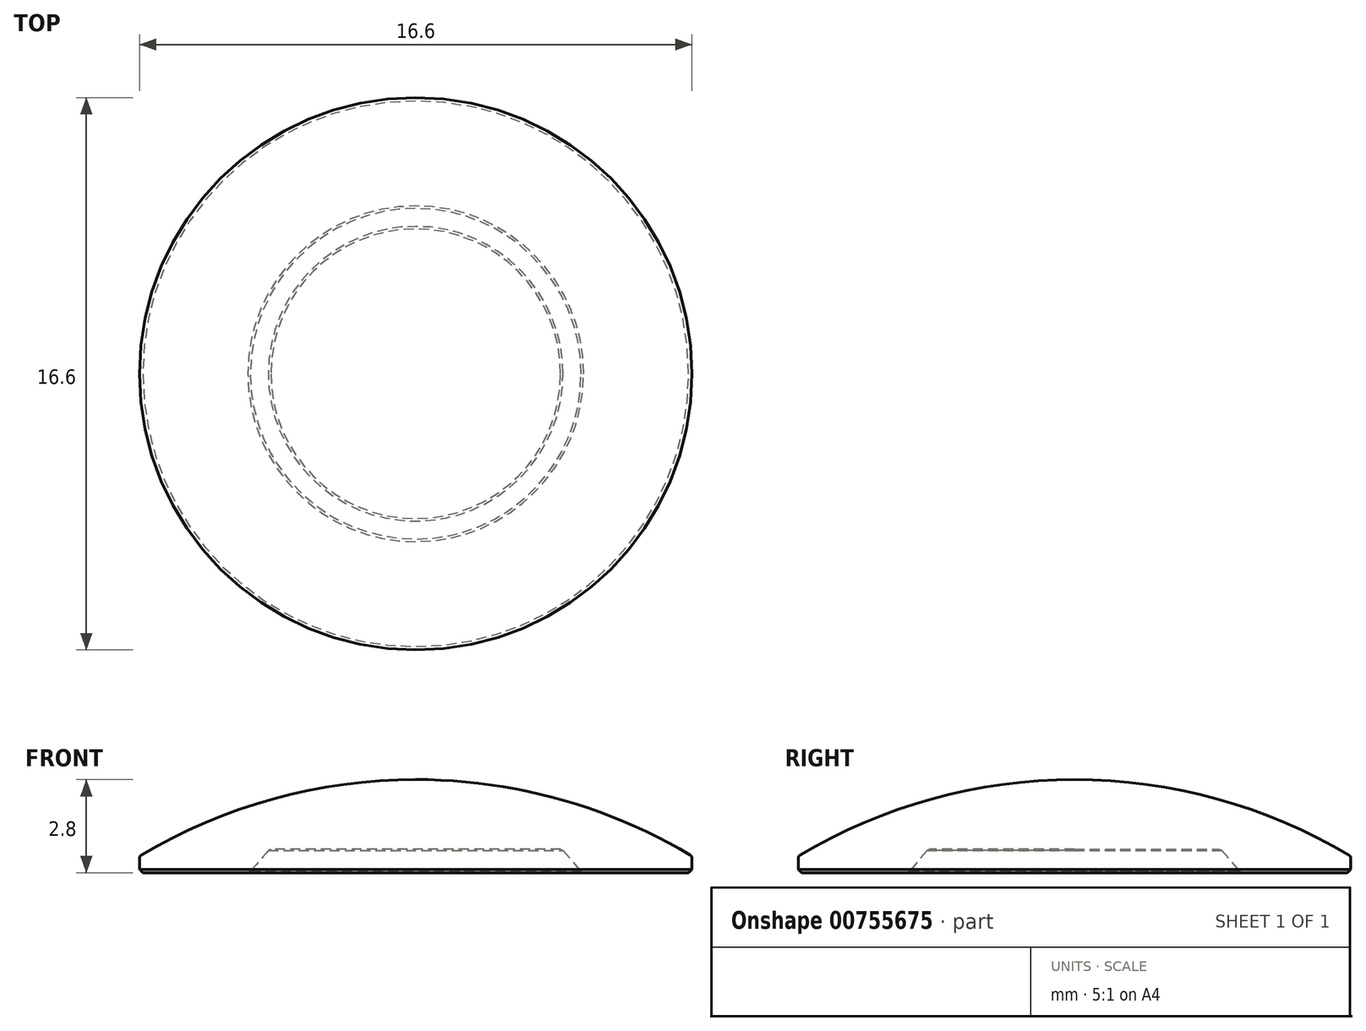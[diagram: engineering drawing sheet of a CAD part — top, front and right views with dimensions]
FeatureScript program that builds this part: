
annotation { "Feature Type Name" : "Feature", "Feature Type Description" : "" }
export const myFeature = defineFeature(function(context is Context, id is Id, definition is map)
    precondition{}
    {
        {
            var Q0;
            Q0=qCreatedBy(makeId("Front.planeOp"),FACE);
            var sketch = newSketch(context, id + "F0", { "sketchPlane" : qUnion([Q0])});
            skLineSegment(sketch, "E0", {"start": v(0, 2.8) * mm, "end": v(12.91, 2.8) * mm, "construction": true});
            skLineSegment(sketch, "E1", {"start": v(8.3, 0) * mm, "end": v(8.3, 0.5) * mm});
            skArc(sketch, "E2", {"start": v(8.3, 0.5) * mm, "mid": v(4.3, 2.21) * mm, "end": v(0, 2.8) * mm});
            skLineSegment(sketch, "E3", {"start": v(8.3, 0) * mm, "end": v(5, 0) * mm});
            skLineSegment(sketch, "E4", {"start": v(0, 2.8) * mm, "end": v(0, 0.7) * mm});
            skLineSegment(sketch, "E5", {"start": v(0, 0.7) * mm, "end": v(4.4, 0.7) * mm});
            skLineSegment(sketch, "E6", {"start": v(4.4, 0.7) * mm, "end": v(5, 0) * mm});
            skLineSegment(sketch, "E7", {"start": v(0, 4.27) * mm, "end": v(0, -3.75) * mm, "construction": true});
            skSolve(sketch);
        }
        {
            var Q0;
            Q0=makeQuery(id+"F0.imprint","IMPRINT",FACE,{"disambiguationData":[TD([[makeQuery(id+"F0.imprint","IMPRINT",EDGE,{"derivedFrom":sQuery(id+"F0.wireOp",EDGE,"E1")}),1.0]])]});
            var Q1;
            Q1=sQuery(id+"F0.wireOp",EDGE,"E7");
            revolve(context, id + "F1", {"surfaceOperationType" : NewSurfaceOperationType.NEW, "entities" : qUnion([Q0]), "axis" : qUnion([Q1]), "revolveType" : RevolveType.FULL});
        }
        {
            var Q0;
            Q0=makeQuery(id+"F1.opRevolve","SWEPT_EDGE",EDGE,{"disambiguationData":[OSD([sQuery(id+"F0.wireOp",EDGE,"E1"),sQuery(id+"F0.wireOp",EDGE,"E3")])]});
            var Q1;
            Q1=makeQuery(id+"F1.opRevolve","SWEPT_EDGE",EDGE,{"disambiguationData":[OSD([sQuery(id+"F0.wireOp",EDGE,"E3"),sQuery(id+"F0.wireOp",EDGE,"E6")])]});
            var Q2;
            Q2=makeQuery(id+"F1.opRevolve","SWEPT_EDGE",EDGE,{"disambiguationData":[OSD([sQuery(id+"F0.wireOp",EDGE,"E5"),sQuery(id+"F0.wireOp",EDGE,"E6")])]});
            chamfer(context, id + "F2", {"entities" : qUnion([Q0, Q1, Q2]), "width" : 0.1 * mm, "tangentPropagation" : true});
        }
        {
            var Q0;
            Q0=makeQuery(id+"F1.opRevolve","SWEPT_EDGE",EDGE,{"disambiguationData":[OSD([sQuery(id+"F0.wireOp",EDGE,"E1"),sQuery(id+"F0.wireOp",EDGE,"E2")])]});
            fillet(context, id + "F3", {"entities" : qUnion([Q0]), "radius" : 0.1 * mm, "tangentPropagation" : true, "allowEdgeOverflow" : false});
        }
    });
